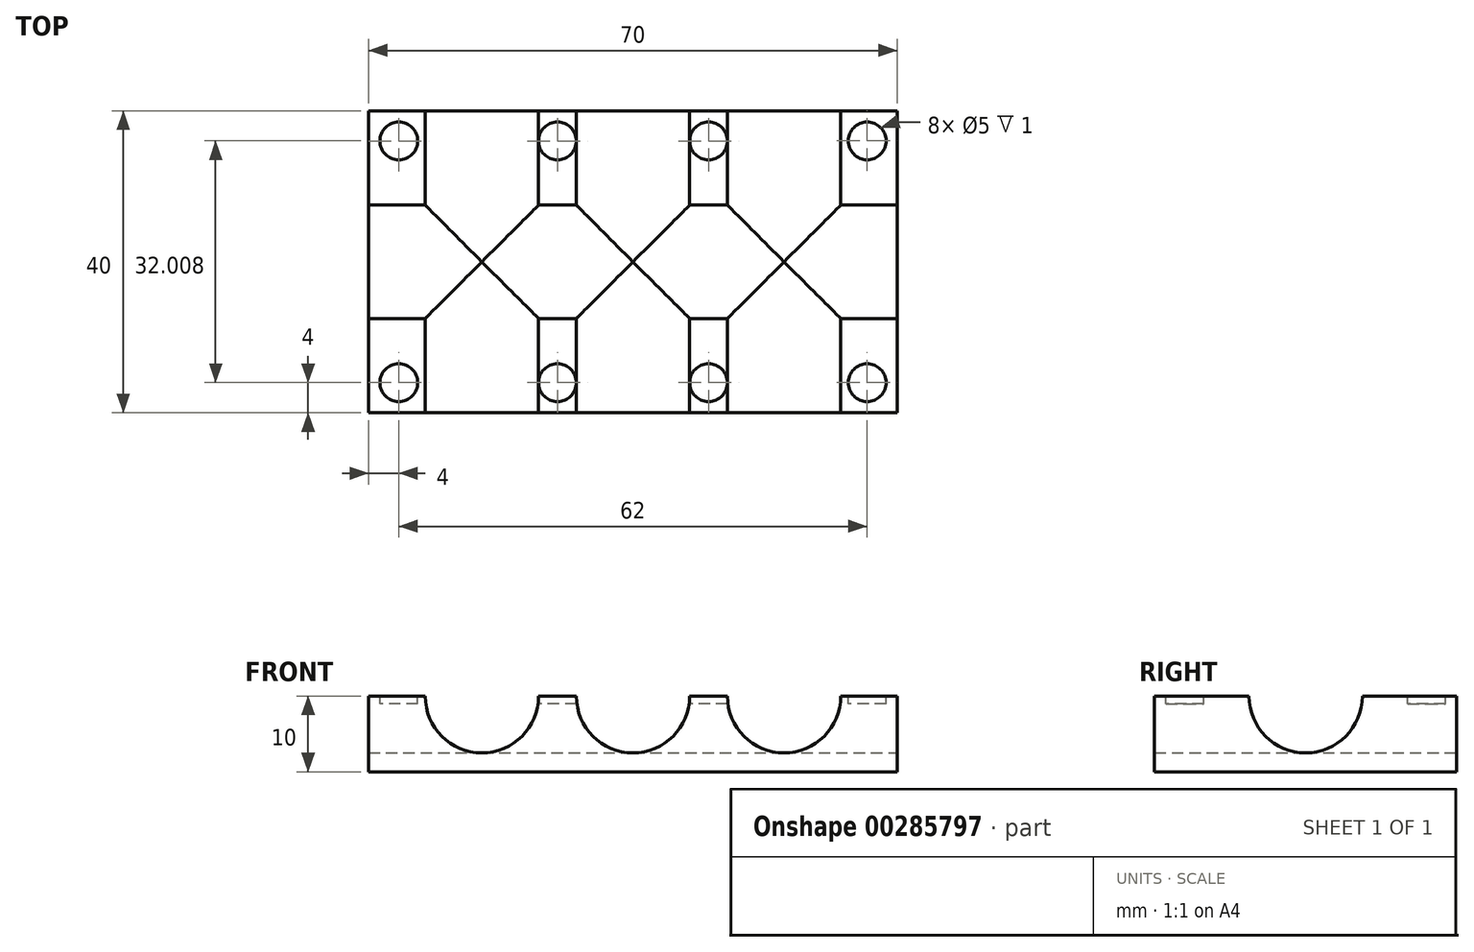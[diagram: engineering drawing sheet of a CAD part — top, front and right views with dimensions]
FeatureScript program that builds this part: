
annotation { "Feature Type Name" : "Feature", "Feature Type Description" : "" }
export const myFeature = defineFeature(function(context is Context, id is Id, definition is map)
    precondition{}
    {
        {
            var Q0;
            Q0=qCreatedBy(makeId("Front.planeOp"),FACE);
            var sketch = newSketch(context, id + "F0", { "sketchPlane" : qUnion([Q0])});
            skLineSegment(sketch, "E0.bottom", {"start": v(35, -5) * mm, "end": v(-35, -5) * mm});
            skLineSegment(sketch, "E0.top", {"start": v(35, 5) * mm, "end": v(-35, 5) * mm});
            skLineSegment(sketch, "E0.left", {"start": v(35, -5) * mm, "end": v(35, 5) * mm});
            skLineSegment(sketch, "E0.right", {"start": v(-35, -5) * mm, "end": v(-35, 5) * mm});
            skPoint(sketch, "E0.middle", {"position": v(0, 0) * mm});
            skPoint(sketch, "E1", {"position": v(-20, 5) * mm});
            skPoint(sketch, "E2", {"position": v(-20, -5) * mm});
            skPoint(sketch, "E3", {"position": v(20, 5) * mm});
            skPoint(sketch, "E4", {"position": v(20, -5) * mm});
            skCircle(sketch, "E5", {"center": v(-20, 5) * mm, "radius": 7.5 * mm});
            skCircle(sketch, "E6", {"center": v(20, 5) * mm, "radius": 7.5 * mm});
            skPoint(sketch, "E7", {"position": v(0, 5) * mm});
            skCircle(sketch, "E8", {"center": v(0, 5) * mm, "radius": 7.5 * mm});
            skSolve(sketch);
        }
        {
            var Q0;
            Q0=makeQuery(id+"F0.imprint","IMPRINT",FACE,{"disambiguationData":[TD([[makeQuery(id+"F0.imprint","IMPRINT",EDGE,{"derivedFrom":sQuery(id+"F0.wireOp",EDGE,"E0.bottom")}),-1.0]])]});
            extrude(context, id + "F1", {"entities" : qUnion([Q0]), "depth" : 40 * mm});
        }
        {
            var Q0;
            Q0=makeQuery(id+"F1.opExtrude","SWEPT_FACE",FACE,{"disambiguationData":[OSD([sQuery(id+"F0.wireOp",EDGE,"E0.left")])]});
            var sketch = newSketch(context, id + "F2", { "sketchPlane" : qUnion([Q0])});
            skPoint(sketch, "E9", {"position": v(-20, 0) * mm});
            skPoint(sketch, "E9.positionSnap0", {"position": v(0, 0) * mm});
            skPoint(sketch, "E10", {"position": v(-20, 5) * mm});
            skCircle(sketch, "E11", {"center": v(-20, 5) * mm, "radius": 7.5 * mm});
            skSolve(sketch);
        }
        {
            var Q0;
            {var subQ0=sQuery(id+"F2.wireOp",EDGE,"E11");var subQ1=makeQuery(id+"F1.opExtrude","SWEPT_EDGE",EDGE,{"disambiguationData":[OSD([sQuery(id+"F0.wireOp",EDGE,"E0.top"),sQuery(id+"F0.wireOp",EDGE,"E0.left")])]});var subQ2=makeQuery(id+"F2.imprint","INTERSECT",VERTEX,{"disambiguationData":[OD(0.0)],"derivedFrom":[subQ1,subQ0]});Q0=makeQuery(id+"F2.imprint","IMPRINT",FACE,{"disambiguationData":[TD([[makeQuery(id+"F2.imprint","IMPRINT",EDGE,{"disambiguationData":[TD([[subQ2,1.0]])],"derivedFrom":subQ0}),1.0]])]});}
            extrude(context, id + "F3", {"entities" : qUnion([Q0]), "operationType" : NewBodyOperationType.REMOVE, "endBound" : BoundingType.THROUGH_ALL, "oppositeDirection" : true, "depth" : 25 * mm});
        }
        {
            var Q0;
            {var subQ0=sQuery(id+"F0.wireOp",EDGE,"E6");var subQ1=sQuery(id+"F0.wireOp",EDGE,"E0.left");var subQ2=sQuery(id+"F0.wireOp",EDGE,"E0.top");Q0=makeQuery(id+"F3.boolean.opBoolean","SPLIT",FACE,{"disambiguationData":[TD([makeQuery(id+"F1.opExtrude","CAP_FACE",FACE,{"disambiguationData":[OSD([sQuery(id+"F0.wireOp",EDGE,"E0.bottom"),subQ2,subQ1,sQuery(id+"F0.wireOp",EDGE,"E0.right"),sQuery(id+"F0.wireOp",EDGE,"E5"),subQ0,sQuery(id+"F0.wireOp",EDGE,"E8")])],"isStart":false})])],"derivedFrom":makeQuery(id+"F1.opExtrude","SWEPT_FACE",FACE,{"disambiguationData":[OSD([subQ2]),TDD([makeQuery(id+"F0.imprint","IMPRINT",EDGE,{"disambiguationData":[TD([[makeQuery(id+"F0.imprint","INTERSECT",VERTEX,{"derivedFrom":[subQ2,subQ1]}),-1.0]])],"derivedFrom":subQ2})])]})});}
            var sketch = newSketch(context, id + "F4", { "sketchPlane" : qUnion([Q0])});
            skPoint(sketch, "E12", {"position": v(31, -36) * mm});
            skPoint(sketch, "E12.positionSnap0", {"position": v(35, -33.75) * mm});
            skCircle(sketch, "E13", {"center": v(31, -36) * mm, "radius": 2.5 * mm});
            skSolve(sketch);
        }
        {
            var Q0;
            Q0=makeQuery(id+"F4.imprint","IMPRINT",FACE,{"disambiguationData":[TD([[makeQuery(id+"F4.imprint","IMPRINT",EDGE,{"derivedFrom":sQuery(id+"F4.wireOp",EDGE,"E13")}),1.0]])]});
            extrude(context, id + "F5", {"entities" : qUnion([Q0]), "operationType" : NewBodyOperationType.REMOVE, "oppositeDirection" : true, "depth" : 1 * mm});
        }
        {
            var Q0;
            {var subQ0=sQuery(id+"F0.wireOp",EDGE,"E6");var subQ1=sQuery(id+"F0.wireOp",EDGE,"E0.left");var subQ2=sQuery(id+"F0.wireOp",EDGE,"E0.top");Q0=makeQuery(id+"F3.boolean.opBoolean","SPLIT",FACE,{"disambiguationData":[TD([makeQuery(id+"F1.opExtrude","CAP_FACE",FACE,{"disambiguationData":[OSD([sQuery(id+"F0.wireOp",EDGE,"E0.bottom"),subQ2,subQ1,sQuery(id+"F0.wireOp",EDGE,"E0.right"),sQuery(id+"F0.wireOp",EDGE,"E5"),subQ0,sQuery(id+"F0.wireOp",EDGE,"E8")])],"isStart":true})])],"derivedFrom":makeQuery(id+"F1.opExtrude","SWEPT_FACE",FACE,{"disambiguationData":[OSD([subQ2]),TDD([makeQuery(id+"F0.imprint","IMPRINT",EDGE,{"disambiguationData":[TD([[makeQuery(id+"F0.imprint","INTERSECT",VERTEX,{"derivedFrom":[subQ2,subQ1]}),-1.0]])],"derivedFrom":subQ2})])]})});}
            var sketch = newSketch(context, id + "F6", { "sketchPlane" : qUnion([Q0])});
            skPoint(sketch, "E14", {"position": v(31, -4) * mm});
            skCircle(sketch, "E15", {"center": v(31, -4) * mm, "radius": 2.5 * mm});
            skSolve(sketch);
        }
        {
            var Q0;
            Q0=makeQuery(id+"F6.imprint","IMPRINT",FACE,{"disambiguationData":[TD([[makeQuery(id+"F6.imprint","IMPRINT",EDGE,{"derivedFrom":sQuery(id+"F6.wireOp",EDGE,"E15")}),1.0]])]});
            extrude(context, id + "F7", {"entities" : qUnion([Q0]), "operationType" : NewBodyOperationType.REMOVE, "oppositeDirection" : true, "depth" : 1 * mm});
        }
        {
            var Q0;
            {var subQ0=sQuery(id+"F0.wireOp",EDGE,"E5");var subQ1=sQuery(id+"F0.wireOp",EDGE,"E0.right");var subQ2=sQuery(id+"F0.wireOp",EDGE,"E0.top");Q0=makeQuery(id+"F3.boolean.opBoolean","SPLIT",FACE,{"disambiguationData":[TD([makeQuery(id+"F1.opExtrude","CAP_FACE",FACE,{"disambiguationData":[OSD([sQuery(id+"F0.wireOp",EDGE,"E0.bottom"),subQ2,sQuery(id+"F0.wireOp",EDGE,"E0.left"),subQ1,subQ0,sQuery(id+"F0.wireOp",EDGE,"E6"),sQuery(id+"F0.wireOp",EDGE,"E8")])],"isStart":false})])],"derivedFrom":makeQuery(id+"F1.opExtrude","SWEPT_FACE",FACE,{"disambiguationData":[OSD([subQ2]),TDD([makeQuery(id+"F0.imprint","IMPRINT",EDGE,{"disambiguationData":[TD([[makeQuery(id+"F0.imprint","INTERSECT",VERTEX,{"derivedFrom":[subQ2,subQ1]}),1.0]])],"derivedFrom":subQ2})])]})});}
            var sketch = newSketch(context, id + "F8", { "sketchPlane" : qUnion([Q0])});
            skPoint(sketch, "E16", {"position": v(-31, -36) * mm});
            skCircle(sketch, "E17", {"center": v(-31, -36) * mm, "radius": 2.5 * mm});
            skSolve(sketch);
        }
        {
            var Q0;
            Q0=makeQuery(id+"F8.imprint","IMPRINT",FACE,{"disambiguationData":[TD([[makeQuery(id+"F8.imprint","IMPRINT",EDGE,{"derivedFrom":sQuery(id+"F8.wireOp",EDGE,"E17")}),1.0]])]});
            extrude(context, id + "F9", {"entities" : qUnion([Q0]), "operationType" : NewBodyOperationType.REMOVE, "oppositeDirection" : true, "depth" : 1 * mm});
        }
        {
            var Q0;
            {var subQ0=sQuery(id+"F0.wireOp",EDGE,"E5");var subQ1=sQuery(id+"F0.wireOp",EDGE,"E0.right");var subQ2=sQuery(id+"F0.wireOp",EDGE,"E0.top");Q0=makeQuery(id+"F3.boolean.opBoolean","SPLIT",FACE,{"disambiguationData":[TD([makeQuery(id+"F1.opExtrude","CAP_FACE",FACE,{"disambiguationData":[OSD([sQuery(id+"F0.wireOp",EDGE,"E0.bottom"),subQ2,sQuery(id+"F0.wireOp",EDGE,"E0.left"),subQ1,subQ0,sQuery(id+"F0.wireOp",EDGE,"E6"),sQuery(id+"F0.wireOp",EDGE,"E8")])],"isStart":true})])],"derivedFrom":makeQuery(id+"F1.opExtrude","SWEPT_FACE",FACE,{"disambiguationData":[OSD([subQ2]),TDD([makeQuery(id+"F0.imprint","IMPRINT",EDGE,{"disambiguationData":[TD([[makeQuery(id+"F0.imprint","INTERSECT",VERTEX,{"derivedFrom":[subQ2,subQ1]}),1.0]])],"derivedFrom":subQ2})])]})});}
            var sketch = newSketch(context, id + "F10", { "sketchPlane" : qUnion([Q0])});
            skPoint(sketch, "E18", {"position": v(-31, -4) * mm});
            skCircle(sketch, "E19", {"center": v(-31, -4) * mm, "radius": 2.5 * mm});
            skSolve(sketch);
        }
        {
            var Q0;
            Q0=makeQuery(id+"F10.imprint","IMPRINT",FACE,{"disambiguationData":[TD([[makeQuery(id+"F10.imprint","IMPRINT",EDGE,{"derivedFrom":sQuery(id+"F10.wireOp",EDGE,"E19")}),1.0]])]});
            extrude(context, id + "F11", {"entities" : qUnion([Q0]), "operationType" : NewBodyOperationType.REMOVE, "oppositeDirection" : true, "depth" : 1 * mm});
        }
        {
            var Q0;
            {var subQ0=sQuery(id+"F0.wireOp",EDGE,"E8");var subQ1=sQuery(id+"F0.wireOp",EDGE,"E5");var subQ2=sQuery(id+"F0.wireOp",EDGE,"E0.top");Q0=makeQuery(id+"F3.boolean.opBoolean","SPLIT",FACE,{"disambiguationData":[TD([makeQuery(id+"F1.opExtrude","CAP_FACE",FACE,{"disambiguationData":[OSD([sQuery(id+"F0.wireOp",EDGE,"E0.bottom"),subQ2,sQuery(id+"F0.wireOp",EDGE,"E0.left"),sQuery(id+"F0.wireOp",EDGE,"E0.right"),subQ1,sQuery(id+"F0.wireOp",EDGE,"E6"),subQ0])],"isStart":true})])],"derivedFrom":makeQuery(id+"F1.opExtrude","SWEPT_FACE",FACE,{"disambiguationData":[OSD([subQ2]),TDD([makeQuery(id+"F0.imprint","IMPRINT",EDGE,{"disambiguationData":[TD([[makeQuery(id+"F0.imprint","INTERSECT",VERTEX,{"disambiguationData":[OD(1.0)],"derivedFrom":[subQ2,subQ0]}),-1.0]])],"derivedFrom":subQ2})])]})});}
            var sketch = newSketch(context, id + "F12", { "sketchPlane" : qUnion([Q0])});
            skPoint(sketch, "E20", {"position": v(-10, -4) * mm});
            skCircle(sketch, "E21", {"center": v(-10, -4) * mm, "radius": 2.5 * mm});
            skSolve(sketch);
        }
        {
            var Q0;
            {var subQ0=sQuery(id+"F12.wireOp",EDGE,"E21");var subQ1=sQuery(id+"F0.wireOp",EDGE,"E8");var subQ2=sQuery(id+"F0.wireOp",EDGE,"E5");var subQ3=sQuery(id+"F0.wireOp",EDGE,"E0.top");var subQ4=makeQuery(id+"F1.opExtrude","CAP_FACE",FACE,{"disambiguationData":[OSD([sQuery(id+"F0.wireOp",EDGE,"E0.bottom"),subQ3,sQuery(id+"F0.wireOp",EDGE,"E0.left"),sQuery(id+"F0.wireOp",EDGE,"E0.right"),subQ2,sQuery(id+"F0.wireOp",EDGE,"E6"),subQ1])],"isStart":true});var subQ5=makeQuery(id+"F0.imprint","INTERSECT",VERTEX,{"disambiguationData":[OD(1.0)],"derivedFrom":[subQ3,subQ1]});var subQ9=makeQuery(id+"F12.imprint","INTERSECT",VERTEX,{"derivedFrom":[makeQuery(id+"F3.boolean.opBoolean","SPLIT",EDGE,{"disambiguationData":[TD([subQ4])],"derivedFrom":makeQuery(id+"F1.opExtrude","SWEPT_EDGE",EDGE,{"disambiguationData":[OSD([subQ3,subQ1]),TDD([subQ5])]})}),subQ0]});Q0=makeQuery(id+"F12.imprint","IMPRINT",FACE,{"disambiguationData":[TD([[makeQuery(id+"F12.imprint","IMPRINT",EDGE,{"disambiguationData":[TD([[subQ9,-1.0]])],"derivedFrom":subQ0}),1.0]])]});}
            extrude(context, id + "F13", {"entities" : qUnion([Q0]), "operationType" : NewBodyOperationType.REMOVE, "oppositeDirection" : true, "depth" : 1 * mm});
        }
        {
            var Q0;
            {var subQ0=sQuery(id+"F0.wireOp",EDGE,"E8");var subQ1=sQuery(id+"F0.wireOp",EDGE,"E6");var subQ2=sQuery(id+"F0.wireOp",EDGE,"E0.top");Q0=makeQuery(id+"F3.boolean.opBoolean","SPLIT",FACE,{"disambiguationData":[TD([makeQuery(id+"F1.opExtrude","CAP_FACE",FACE,{"disambiguationData":[OSD([sQuery(id+"F0.wireOp",EDGE,"E0.bottom"),subQ2,sQuery(id+"F0.wireOp",EDGE,"E0.left"),sQuery(id+"F0.wireOp",EDGE,"E0.right"),sQuery(id+"F0.wireOp",EDGE,"E5"),subQ1,subQ0])],"isStart":true})])],"derivedFrom":makeQuery(id+"F1.opExtrude","SWEPT_FACE",FACE,{"disambiguationData":[OSD([subQ2]),TDD([makeQuery(id+"F0.imprint","IMPRINT",EDGE,{"disambiguationData":[TD([[makeQuery(id+"F0.imprint","INTERSECT",VERTEX,{"disambiguationData":[OD(1.0)],"derivedFrom":[subQ2,subQ1]}),-1.0]])],"derivedFrom":subQ2})])]})});}
            var sketch = newSketch(context, id + "F14", { "sketchPlane" : qUnion([Q0])});
            skPoint(sketch, "E22", {"position": v(10, -4) * mm});
            skCircle(sketch, "E23", {"center": v(10, -4) * mm, "radius": 2.5 * mm});
            skSolve(sketch);
        }
        {
            var Q0;
            {var subQ0=sQuery(id+"F14.wireOp",EDGE,"E23");var subQ1=sQuery(id+"F0.wireOp",EDGE,"E8");var subQ2=sQuery(id+"F0.wireOp",EDGE,"E6");var subQ3=sQuery(id+"F0.wireOp",EDGE,"E0.top");var subQ4=makeQuery(id+"F1.opExtrude","CAP_FACE",FACE,{"disambiguationData":[OSD([sQuery(id+"F0.wireOp",EDGE,"E0.bottom"),subQ3,sQuery(id+"F0.wireOp",EDGE,"E0.left"),sQuery(id+"F0.wireOp",EDGE,"E0.right"),sQuery(id+"F0.wireOp",EDGE,"E5"),subQ2,subQ1])],"isStart":true});var subQ5=makeQuery(id+"F0.imprint","INTERSECT",VERTEX,{"disambiguationData":[OD(1.0)],"derivedFrom":[subQ3,subQ2]});var subQ9=makeQuery(id+"F14.imprint","INTERSECT",VERTEX,{"derivedFrom":[makeQuery(id+"F3.boolean.opBoolean","SPLIT",EDGE,{"disambiguationData":[TD([subQ4])],"derivedFrom":makeQuery(id+"F1.opExtrude","SWEPT_EDGE",EDGE,{"disambiguationData":[OSD([subQ3,subQ2]),TDD([subQ5])]})}),subQ0]});Q0=makeQuery(id+"F14.imprint","IMPRINT",FACE,{"disambiguationData":[TD([[makeQuery(id+"F14.imprint","IMPRINT",EDGE,{"disambiguationData":[TD([[subQ9,-1.0]])],"derivedFrom":subQ0}),1.0]])]});}
            extrude(context, id + "F15", {"entities" : qUnion([Q0]), "operationType" : NewBodyOperationType.REMOVE, "oppositeDirection" : true, "depth" : 1 * mm});
        }
        {
            var Q0;
            {var subQ0=sQuery(id+"F0.wireOp",EDGE,"E8");var subQ1=sQuery(id+"F0.wireOp",EDGE,"E5");var subQ2=sQuery(id+"F0.wireOp",EDGE,"E0.top");Q0=makeQuery(id+"F3.boolean.opBoolean","SPLIT",FACE,{"disambiguationData":[TD([makeQuery(id+"F1.opExtrude","CAP_FACE",FACE,{"disambiguationData":[OSD([sQuery(id+"F0.wireOp",EDGE,"E0.bottom"),subQ2,sQuery(id+"F0.wireOp",EDGE,"E0.left"),sQuery(id+"F0.wireOp",EDGE,"E0.right"),subQ1,sQuery(id+"F0.wireOp",EDGE,"E6"),subQ0])],"isStart":false})])],"derivedFrom":makeQuery(id+"F1.opExtrude","SWEPT_FACE",FACE,{"disambiguationData":[OSD([subQ2]),TDD([makeQuery(id+"F0.imprint","IMPRINT",EDGE,{"disambiguationData":[TD([[makeQuery(id+"F0.imprint","INTERSECT",VERTEX,{"disambiguationData":[OD(1.0)],"derivedFrom":[subQ2,subQ0]}),-1.0]])],"derivedFrom":subQ2})])]})});}
            var sketch = newSketch(context, id + "F16", { "sketchPlane" : qUnion([Q0])});
            skPoint(sketch, "E24", {"position": v(-10, -36) * mm});
            skCircle(sketch, "E25", {"center": v(-10, -36) * mm, "radius": 2.5 * mm});
            skSolve(sketch);
        }
        {
            var Q0;
            {var subQ0=sQuery(id+"F16.wireOp",EDGE,"E25");var subQ1=sQuery(id+"F0.wireOp",EDGE,"E8");var subQ2=sQuery(id+"F0.wireOp",EDGE,"E5");var subQ3=sQuery(id+"F0.wireOp",EDGE,"E0.top");var subQ4=makeQuery(id+"F1.opExtrude","CAP_FACE",FACE,{"disambiguationData":[OSD([sQuery(id+"F0.wireOp",EDGE,"E0.bottom"),subQ3,sQuery(id+"F0.wireOp",EDGE,"E0.left"),sQuery(id+"F0.wireOp",EDGE,"E0.right"),subQ2,sQuery(id+"F0.wireOp",EDGE,"E6"),subQ1])],"isStart":false});var subQ5=makeQuery(id+"F0.imprint","INTERSECT",VERTEX,{"disambiguationData":[OD(1.0)],"derivedFrom":[subQ3,subQ1]});var subQ9=makeQuery(id+"F16.imprint","INTERSECT",VERTEX,{"derivedFrom":[makeQuery(id+"F3.boolean.opBoolean","SPLIT",EDGE,{"disambiguationData":[TD([subQ4])],"derivedFrom":makeQuery(id+"F1.opExtrude","SWEPT_EDGE",EDGE,{"disambiguationData":[OSD([subQ3,subQ1]),TDD([subQ5])]})}),subQ0]});Q0=makeQuery(id+"F16.imprint","IMPRINT",FACE,{"disambiguationData":[TD([[makeQuery(id+"F16.imprint","IMPRINT",EDGE,{"disambiguationData":[TD([[subQ9,-1.0]])],"derivedFrom":subQ0}),1.0]])]});}
            extrude(context, id + "F17", {"entities" : qUnion([Q0]), "operationType" : NewBodyOperationType.REMOVE, "oppositeDirection" : true, "depth" : 1 * mm});
        }
        {
            var Q0;
            {var subQ0=sQuery(id+"F0.wireOp",EDGE,"E8");var subQ1=sQuery(id+"F0.wireOp",EDGE,"E6");var subQ2=sQuery(id+"F0.wireOp",EDGE,"E0.top");Q0=makeQuery(id+"F3.boolean.opBoolean","SPLIT",FACE,{"disambiguationData":[TD([makeQuery(id+"F1.opExtrude","CAP_FACE",FACE,{"disambiguationData":[OSD([sQuery(id+"F0.wireOp",EDGE,"E0.bottom"),subQ2,sQuery(id+"F0.wireOp",EDGE,"E0.left"),sQuery(id+"F0.wireOp",EDGE,"E0.right"),sQuery(id+"F0.wireOp",EDGE,"E5"),subQ1,subQ0])],"isStart":false})])],"derivedFrom":makeQuery(id+"F1.opExtrude","SWEPT_FACE",FACE,{"disambiguationData":[OSD([subQ2]),TDD([makeQuery(id+"F0.imprint","IMPRINT",EDGE,{"disambiguationData":[TD([[makeQuery(id+"F0.imprint","INTERSECT",VERTEX,{"disambiguationData":[OD(1.0)],"derivedFrom":[subQ2,subQ1]}),-1.0]])],"derivedFrom":subQ2})])]})});}
            var sketch = newSketch(context, id + "F18", { "sketchPlane" : qUnion([Q0])});
            skPoint(sketch, "E26", {"position": v(10, -36) * mm});
            skCircle(sketch, "E27", {"center": v(10, -36) * mm, "radius": 2.5 * mm});
            skSolve(sketch);
        }
        {
            var Q0;
            {var subQ0=sQuery(id+"F18.wireOp",EDGE,"E27");var subQ1=sQuery(id+"F0.wireOp",EDGE,"E8");var subQ2=sQuery(id+"F0.wireOp",EDGE,"E6");var subQ3=sQuery(id+"F0.wireOp",EDGE,"E0.top");var subQ4=makeQuery(id+"F1.opExtrude","CAP_FACE",FACE,{"disambiguationData":[OSD([sQuery(id+"F0.wireOp",EDGE,"E0.bottom"),subQ3,sQuery(id+"F0.wireOp",EDGE,"E0.left"),sQuery(id+"F0.wireOp",EDGE,"E0.right"),sQuery(id+"F0.wireOp",EDGE,"E5"),subQ2,subQ1])],"isStart":false});var subQ5=makeQuery(id+"F0.imprint","INTERSECT",VERTEX,{"disambiguationData":[OD(1.0)],"derivedFrom":[subQ3,subQ2]});var subQ9=makeQuery(id+"F18.imprint","INTERSECT",VERTEX,{"derivedFrom":[makeQuery(id+"F3.boolean.opBoolean","SPLIT",EDGE,{"disambiguationData":[TD([subQ4])],"derivedFrom":makeQuery(id+"F1.opExtrude","SWEPT_EDGE",EDGE,{"disambiguationData":[OSD([subQ3,subQ2]),TDD([subQ5])]})}),subQ0]});Q0=makeQuery(id+"F18.imprint","IMPRINT",FACE,{"disambiguationData":[TD([[makeQuery(id+"F18.imprint","IMPRINT",EDGE,{"disambiguationData":[TD([[subQ9,-1.0]])],"derivedFrom":subQ0}),1.0]])]});}
            extrude(context, id + "F19", {"entities" : qUnion([Q0]), "operationType" : NewBodyOperationType.REMOVE, "oppositeDirection" : true, "depth" : 1 * mm});
        }
    });
